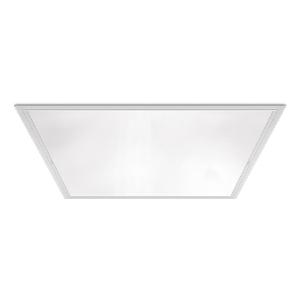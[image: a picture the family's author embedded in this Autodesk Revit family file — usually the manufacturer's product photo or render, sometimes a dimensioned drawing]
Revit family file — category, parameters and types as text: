
# Revit family: 3f_filippi_-_l_340_luce_diffusa_lgs_ip65v_3f_filippi_-_23980_-_l_340_45w-840_dali_lgs_ip65v_596x596
name_source: partatom
category: Lighting Fixtures
units: mm (PartAtom-declared; Revit-internal decimal feet)

## family parameters
Cut with Voids When Loaded = No
Host = Face
Light Source = No
Part Type = Normal
Room Calculation Point = No
Round Connector Dimension = Use Diameter
Shared = No

## types (1)
- 3F Filippi - L 340 Luce Diffusa LGS IP65V (1 x LED, 6537 lm, 50 W, 4000 K)
    Apparent Load = 50 VA
    Approval mark = ENEC
    CIE Flux Codes = 67 92 98 100 100
    Color Rendering = 80
    Color Temperature = 4000 K
    Control Gear = Electronic transformer
    Default Elevation = 1800 mm
    Description = ILLUMINOTECHNICAL
Luminous efficiency 100% (DLOR 100%, ULOR 0%).
Initial luminous flux of the luminaire 6537 lm.
Direct symmetric distribution.
Installation Interdistance Transv.D = 1.19 x hu - Long.D = 1.17 x hu.
Average luminance <3000 cd/m² for radial angles >65°.
Tabular UGR (CIE 117 - 4H-8H; S=0.25H; 70/50/20): RUG 18.3 - 18.3.
Beam angle: 87° - 86°.
Luminous efficacy 131 lm/W.
Lifetime (L93/B10): 30000 h. (tq+25°C)
Lifetime (L90/B10): 50000 h. (tq+25°C)
Lifetime (L85/B10): 80000 h. (tq+25°C)
Lifetime (L80/B10): 100000 h. (tq+25°C)
Sudden decreased luminous flux after 50000 hours: 0% (C0).
Photobiological safety in compliance with IEC/TR 62778: RG0 risk exempt, (IEC 62471).
In compliance with IEC/EN 62722-2-1 - IEC/EN 62717 standards.

SOURCE
Squared LED module 45W/840.
Energy efficiency class (UE 2019/2020 - UE 2019/2015): C.
CIE 13.3 Colour rendering index: CRI >80 (R9 <50%).
IES TM-30 Fidelity Index: Rf = 84 Rg = 95.
CCT nominal colour temperature 4000 K.
Colour initial tolerance (MacAdam): SDCM 3.

MECHANICAL
Housing in hot-galvanised steel, painted in white polyester.
Perimetral frame in white polycarbonate.
LGS micro-prismatic flat diffuser in transparent methacrylate (PMMA), multi-lenticular exterior, anti-glare.
Anti-glare opal polycarbonate filter for brightness uniformity.
Luminaire with limited surface temperature. - D - (EN 60598-2-24)
Dimensions: 596x596 mm, height 80 mm. Weight 4.45 kg.
IP65 protection degree for exposed part, IP40 for recessed part.
Mechanical strength to impacts IK06 (1 joule).
Glow-wire test resistance 650°C.

ELECTRICAL
Wiring on a separate unit.
Halogen Free DALI-2 DATI (Parts 251, 252, 253), PUSH-DIM, electronic wiring 230V-50/60Hz, power factor 0.95 at full load, THD <25%, constant output current, SELV, class II, 1 driver, 1 DALI addresse.
Power of the luminaire 50 W.
CE - IEC 60598-1 - EN 60598-1.
SAFE FLICKER: PstLM=<1 and SVM=<0.4 (IEC TR 61547-1 and IEC TR 63158), to ensure a more comfortable and safe light.
Luminaire compliant with EN 60598-2-22 for power supply from a centralised emergency system CPSS (Central Power Supply System), not incorporated in the luminaire - high risk areas excluded. The default power and flux are 100% in AC and 15% in DC.
Ambient temperature from 0°C to +40°C.
Temperature class T6 max 85°C.
Relative humidity UR: <85%.

INSTALLATION
Lay-on or pull-up recessed fitting using frame accessory.
All accessories dedicated to this product are available on the Catalog and on our website www.3F-Filippi.com.

APPLICATIONS
Suitable product for food production plants (HACCP), IFS (Food Version 6), BRC (GSFS Food Version 7).
In environments requiring protection and simplified cleaning.
Hospitals, pharmaceutical, chemical, aseptic laboratories, sterilised rooms.
Environments: with VDTs, meeting rooms, offices.
Environments: architectural, commercial, staterooms, banks.
Environments where demanding visual tasks are performed and soft diffuse light is required for optimal visual comfort and total shielding of the light source.

LIGHT MANAGEMENT
Recommended minimum setting: 10%.
The luminaire, equipped with (DALI-2 DATI) driver, can be controlled manually with 3F Easy Dim technology or automatically/manually with wired or wireless DALI/D2D control systems.
The D2D driver guarantees interoperability with other devices with the same certification by making the following information available:
Device Data (Part 251), Energy Report (Part 252), Diagnosis & Maintenance (Part 253).
In electrical systems without a regulation system (manual or automatic) and DALI bus, a suitable jumper must be made on the DA-DA terminals of the appliance.

WARNING
Luminaire designed for disposal/recycling at end-of-life.
Replaceable (LED only) light source by a professional. Replaceable control gear by a professional.
    Height = 0 mm  [stored 0 ft]
    Lamp = 1 x LED
    Lamp Light Flux = 6537 lm
    Lamp Power = 50 W
    Lamp count = 1
    Length = 596 mm
    Lifetime = 50000 h
    Luminous efficacy = 131 lm/W
    Manufacturer = 3F Filippi
    ModVariant = No
    Model = 3F Filippi - 23980 - L 340 45W-840 DALI LGS IP65V 596x596
    Mounting Place = Ceiling
    Mounting Type = Recessed
    Number of Poles = 1
    OnlyDefault = Yes
    Power Factor = 1
    Product Name = 3F Filippi - L 340 Luce Diffusa LGS IP65V
    Product group = recessed luminaire
    ProductGroupID = 4
    Protection Class = Protection class II
    Protection Degree = IP 40
    RLX_Detail_Level = 1
    RLX_Emergency_Light_Flux = 0 lm
    RLX_Emergency_Type = 0
    RLX_Emergency_Type_DB = No
    RlxData = <blob elided: 156617 chars, md5=7dba897e>
    Socket = socket
    Standby Power = 0 W
    System Light Flux = 6537 lm
    System Power = 50 W
    Type Comments = Product without accessories
    Type Image = 3ffilippi_l_340_luce_diffusa_lgs_ip65v.jpg
    URL = http://relux.com
    VarID = ---
    Voltage = 0 V
    Weight = 0.00 kg
    Width = 596 mm

note: [stored X ft] marks values corroborated as IEEE doubles in the binary element streams (Revit-internal decimal feet)

## geometry (parser evidence)
native form markers: Blend x4, Sweep x11
no freeform markers — native parametric forms only
